# Revit family: Thorn RACE Wall
name_source: partatom
category: Lighting Fixtures
revit_build: Autodesk Revit 2016 (Build: 20150220_1215(x64)
units: mm (PartAtom-declared; Revit-internal decimal feet)

## family parameters
Cut with Voids When Loaded = No
Host = Face
Light Source = Yes
OmniClass Number = 23.80.70.14
OmniClass Title = Luminaries for External Lighting
Part Type = Normal
Room Calculation Point = No
Round Connector Dimension = Use Diameter
Shared = No

## types (2) — shared parameters
Assembly Code = D5020200
Body = Thorn_Metal_Dark_Grey
Color Filter = 16777215
Description = LED wall grazer
Dimming Lamp Color Temperature Shift = <None>
Lamp = LED
Manufacturer = Thorn Lighting
Metal = Thorn_Metal_Grey
Reflector = Thorn_Cover_Self_llumination
Tilt Angle = 45.00°
Voltage = 230 V
zero-valued in all types: Default Elevation

## per-type parameters (varying)
| type | Apparent Load | Height | Length | Light Source Offset | Model | Photometric Web File | Raze Large | Raze Small | URL | Width |
| RAA Small | 6 VA | 70 mm  [stored 0.229659 ft] | 86 mm  [stored 0.282152 ft] | 85 mm  [stored 0.278871 ft] | 96632095 | TL_RAAS1L35-830.IES | No | Yes | www.thornlighting.com/96632095 | 110 mm  [stored 0.360892 ft] |
| RAA Large | 21 VA | 148 mm  [stored 0.485564 ft] | 204 mm | 150 mm | 96631721 | TL_RAAL1L50-830.IES | Yes | No | www.thornlighting.com/96631721 | 220 mm  [stored 0.721785 ft] |

note: [stored X ft] marks values corroborated as IEEE doubles in the binary element streams (Revit-internal decimal feet)

## geometry (parser evidence)
native form markers: Sweep x7
no freeform markers — native parametric forms only
